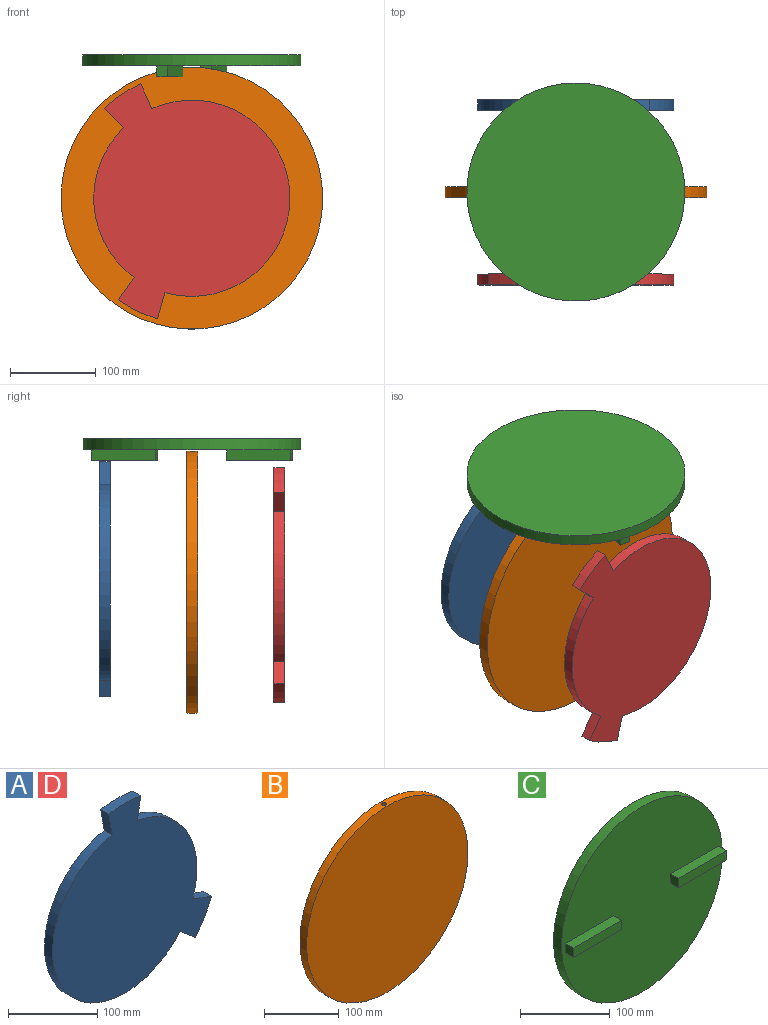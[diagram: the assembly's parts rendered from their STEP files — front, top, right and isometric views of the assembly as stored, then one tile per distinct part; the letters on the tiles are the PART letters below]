
ASSEMBLY  parts=4 mates=2
PART A: 10 faces, bbox 251.5x12.7x260.4 mm
  f0: plane 29.84x12.7mm, normal (0.34,0,0.94), area 403.2mm2, adj f1,f7,f8,f9
  f1: cylinder r=114.3mm len=151.66mm, axis (0,1,0), area 2533.5mm2, adj f0,f2,f8,f9
  f2: plane 31.27x12.7mm, normal (0.98,0,-0.17), area 403.2mm2, adj f1,f3,f8,f9
  f3: cylinder r=146.05mm len=50.72mm, axis (0,1,0), area 647.5mm2, adj f2,f4,f8,f9
  f4: plane 31.27x12.7mm, normal (-0.98,0,-0.17), area 403.2mm2, adj f3,f5,f8,f9
  f5: cylinder r=114.3mm len=226.86mm, axis (0,1,0), area 5573.8mm2, adj f4,f6,f8,f9
  f6: plane 24.32x20.41mm, normal (-0.64,0,-0.77), area 403.2mm2, adj f5,f7,f8,f9
  f7: cylinder r=146.05mm len=43.93mm, axis (0,1,0), area 647.5mm2, adj f0,f6,f8,f9
  f8: plane 260.35x251.54mm, normal (0,-1,0), area 43928.7mm2, adj f0,f1,f2,f3,f4,f5,f6,f7
  f9: plane 260.35x251.54mm, normal (0,1,0), area 43928.7mm2, adj f0,f1,f2,f3,f4,f5,f6,f7
PART B: 4 faces, bbox 304.8x12.7x304.8 mm
  f0: cylinder r=152.4mm len=304.8mm, axis (0,1,0), area 12096.4mm2, adj f1,f2,f3
  f1: plane 304.8x304.8mm, normal (0,-1,0), area 72965.9mm2, adj f0
  f2: plane 304.8x304.8mm, normal (0,1,0), area 72965.9mm2, adj f0
  f3: cylinder r=3.2mm len=304.8mm, axis (0,0,-1), area 6128.5mm2, adj f0
PART C: 13 faces, bbox 254x25.4x254 mm
  f0: cylinder r=127mm len=254mm, axis (0,1,0), area 10134.1mm2, adj f1,f2
  f1: plane 254x254mm, normal (0,-1,0), area 48735.3mm2, adj f0,f4,f5,f6,f7,f9,f10,f11
  f2: plane 254x254mm, normal (0,1,0), area 50670.7mm2, adj f0
  f3: plane 76.2x12.7mm, normal (0,-1,0), area 967.7mm2, adj f4,f5,f6,f7
  f4: plane 12.7x12.7mm, normal (1,0,0), area 161.3mm2, adj f1,f3,f5,f7
  f5: plane 76.2x12.7mm, normal (0,0,1), area 967.7mm2, adj f1,f3,f4,f6
  f6: plane 12.7x12.7mm, normal (-1,0,0), area 161.3mm2, adj f1,f3,f5,f7
  f7: plane 76.2x12.7mm, normal (0,0,-1), area 967.7mm2, adj f1,f3,f4,f6
  f8: plane 76.2x12.7mm, normal (0,-1,0), area 967.7mm2, adj f9,f10,f11,f12
  f9: plane 76.2x12.7mm, normal (0,0,-1), area 967.7mm2, adj f1,f8,f10,f12
  f10: plane 12.7x12.7mm, normal (1,0,0), area 161.3mm2, adj f1,f8,f9,f11
  f11: plane 76.2x12.7mm, normal (0,0,1), area 967.7mm2, adj f1,f8,f10,f12
  f12: plane 12.7x12.7mm, normal (-1,0,0), area 161.3mm2, adj f1,f8,f9,f11
PART D: same geometry as A
PLACE A rot(axis=(0,1,0),25.9deg) t=(-497.48,-38.1,-210.06)mm
PLACE B t=(-660.4,-139.7,-406.4)mm
PLACE C rot(axis=(0.67,0.53,0.53),112.4deg) t=(-635.18,-884.7,14.53)mm
PLACE D rot(axis=(0,-1,0),154.1deg) t=(497.48,-241.3,210.06)mm
MATE revolute C.f0 <-> B.f3  axis (0,0,-1) through (0,6.35,154.23)mm
MATE fastened A.f1 <-> D.f1  axis (0,1,0) through (0,114.3,0)mm
